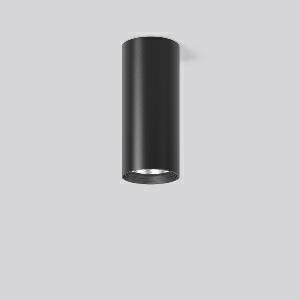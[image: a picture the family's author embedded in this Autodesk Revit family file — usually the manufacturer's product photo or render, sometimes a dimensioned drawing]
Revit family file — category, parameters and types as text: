
# Revit family: heledon_mini_a_931210_003_5561
name_source: partatom
category: Lighting Fixtures
units: mm (PartAtom-declared; Revit-internal decimal feet)

## family parameters
Cut with Voids When Loaded = No
Host = Face
Light Source = No
Part Type = Normal
Room Calculation Point = No
Round Connector Dimension = Use Diameter
Shared = No

## types (1)
- HELEDON mini A (1 x LED Modul 930, 3650 lm, 3000)
    Apparent Load = 29 VA
    Approval mark = CE
    CIE Flux Codes = 95 99 100 100 100
    Color Rendering = 90
    Color Temperature = 3000
    Default Elevation = 1800 mm
    Description = Series: HELEDON mini
Cylindrical surface-mounted downlight. Housing: die-cast aluminium, powder-coated. Internal ceiling frame polycarbonate with bayonet mounting. Black plastic ring and recessed LED to prevent glare from the side. Optical assembly with reflector made of MIRO-Silver with 98% total light reflection for outstanding efficiency - can be changed without tools. Best colour rendering index Ra>90. Suitable for Ceiling mounting. Easy installation with a separate ceiling frame with bayonet mounting and plug connection. Driver integrated. Connected via plug-in connector. High quality converter without flickering and stroboscopic effect. The following accessories can be mounted without use of tools: interchangeable lenses, decorative glasses, honeycomb louvre, clear and frosted diffusers, white interchangeable plastic ring. 
Colour: deep black, matt (RAL 9005)
Diameter: 87 mm
Height: 197 mm
Lamp: LED
Socket: without socket
Colour temperature: 3000K
Colour rendering index (CRI): 92
System power: 29 W
Rated luminous flux: 3650 lm
Luminous efficiency: 126 lm/W
Control gear: Regulated power supply
Protection class: I
Type of protection: IP 20
    Height = 197 mm
    Lamp = 1 x LED Modul 930
    Lamp Light Flux = 3650 lm
    Lamp count = 1
    Length = 87 mm
    Lifetime = 50000 h
    Luminous efficacy = 126 lm/W
    Manufacturer = RZB
    ModVariant = No
    Model = 931210.003
    Mounting Place = Ceiling
    Mounting Type = Surface mounted
    Number of Poles = 1
    OnlyDefault = Yes
    Power Factor = 1
    Product Name = HELEDON mini A
    Product group = Surface mounted downlights
    ProductGroupID = 302
    Protection Class = Protection class I
    Protection Degree = IP 20
    RLX_Detail_Level = 1
    RLX_Emergency_Light_Flux = 0 lm
    RLX_Emergency_Type = 0
    RLX_Emergency_Type_DB = No
    RlxData = <blob elided: 107881 chars, md5=73784811>
    Socket = socket
    Standby Power = 0 W
    System Light Flux = 3650 lm
    System Power = 29 W
    Type Comments = Product without accessories
    Type Image = 931188.003.jpg
    URL = http://relux.com
    VarID = ---
    Voltage = 230 V
    Voltage Range = 220-240 V
    Weight = 0.00 kg
    Width = 0 mm  [stored 0 ft]

note: [stored X ft] marks values corroborated as IEEE doubles in the binary element streams (Revit-internal decimal feet)

## geometry (parser evidence)
native form markers: Blend x4, Sweep x9
no freeform markers — native parametric forms only
